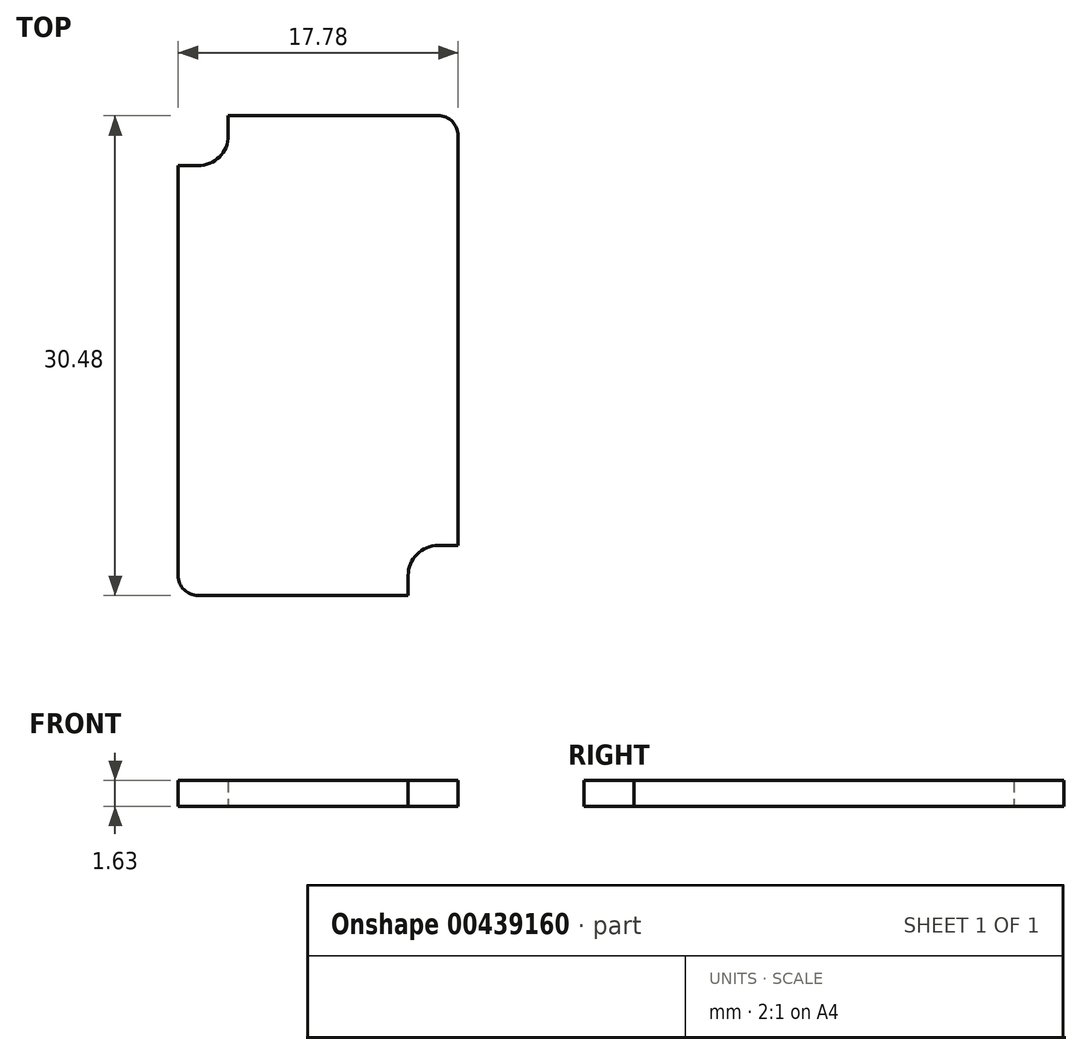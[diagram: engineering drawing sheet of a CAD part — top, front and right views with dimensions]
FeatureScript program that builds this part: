
annotation { "Feature Type Name" : "Feature", "Feature Type Description" : "" }
export const myFeature = defineFeature(function(context is Context, id is Id, definition is map)
    precondition{}
    {
        {
            var Q0;
            Q0=qCreatedBy(makeId("Top.planeOp"),FACE);
            var sketch = newSketch(context, id + "F0", { "sketchPlane" : qUnion([Q0])});
            skLineSegment(sketch, "E0.bottom", {"start": v(7.62, 15.24) * mm, "end": v(-5.72, 15.24) * mm});
            skLineSegment(sketch, "E0.top", {"start": v(5.71, -15.24) * mm, "end": v(-7.62, -15.24) * mm});
            skLineSegment(sketch, "E0.left", {"start": v(8.9, 13.97) * mm, "end": v(8.9, -12.06) * mm});
            skLineSegment(sketch, "E0.right", {"start": v(-8.9, 12.06) * mm, "end": v(-8.9, -13.97) * mm});
            skPoint(sketch, "E0.middle", {"position": v(0, 0) * mm});
            skPoint(sketch, "E1.visualSharp", {"position": v(8.9, 15.24) * mm});
            skArc(sketch, "E1.filletArc", {"start": v(8.9, 13.97) * mm, "mid": v(8.52, 14.87) * mm, "end": v(7.62, 15.24) * mm});
            skPoint(sketch, "E2.visualSharp", {"position": v(-8.9, -15.24) * mm});
            skArc(sketch, "E2.filletArc", {"start": v(-8.9, -13.97) * mm, "mid": v(-8.52, -14.87) * mm, "end": v(-7.62, -15.24) * mm});
            skCircle(sketch, "E3", {"center": v(7.62, -13.97) * mm, "radius": 1.2 * mm, "construction": true});
            skCircle(sketch, "E4", {"center": v(-7.62, 13.97) * mm, "radius": 1.2 * mm, "construction": true});
            skLineSegment(sketch, "E5", {"start": v(-8.9, 12.06) * mm, "end": v(-7.62, 12.06) * mm});
            skLineSegment(sketch, "E6", {"start": v(-5.72, 13.97) * mm, "end": v(-5.72, 15.24) * mm});
            skPoint(sketch, "E7.visualSharp", {"position": v(-5.72, 12.06) * mm});
            skArc(sketch, "E7.filletArc", {"start": v(-7.62, 12.06) * mm, "mid": v(-6.27, 12.62) * mm, "end": v(-5.72, 13.97) * mm});
            skLineSegment(sketch, "E8", {"start": v(8.9, -12.06) * mm, "end": v(7.62, -12.07) * mm});
            skLineSegment(sketch, "E9", {"start": v(5.71, -13.97) * mm, "end": v(5.71, -15.24) * mm});
            skPoint(sketch, "E10.visualSharp", {"position": v(5.71, -12.07) * mm});
            skArc(sketch, "E10.filletArc", {"start": v(7.62, -12.07) * mm, "mid": v(6.27, -12.62) * mm, "end": v(5.71, -13.97) * mm});
            skSolve(sketch);
        }
        {
            var Q0;
            Q0=makeQuery(id+"F0.imprint","IMPRINT",FACE,{"disambiguationData":[TD([[makeQuery(id+"F0.imprint","IMPRINT",EDGE,{"derivedFrom":sQuery(id+"F0.wireOp",EDGE,"E0.bottom")}),1.0]])]});
            extrude(context, id + "F1", {"entities" : qUnion([Q0]), "depth" : 1.63 * mm});
        }
    });
